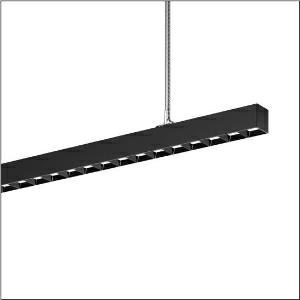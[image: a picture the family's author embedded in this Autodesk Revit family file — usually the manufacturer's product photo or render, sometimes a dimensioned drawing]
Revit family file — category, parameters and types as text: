
# Revit family: silica_r__21_51mx32dc4dbb_b922
name_source: partatom
category: Lighting Fixtures
units: mm (PartAtom-declared; Revit-internal decimal feet)

## family parameters
Cut with Voids When Loaded = No
Host = Face
Light Source = No
Part Type = Normal
Room Calculation Point = No
Round Connector Dimension = Use Diameter
Shared = No

## types (1)
- --- (1 x LED, 18230 lm, 105.8 W, 4000K)
    Apparent Load = 106 VA
    CIE Flux Codes = 86 99 100 59 100
    Color Rendering = 80
    Color Temperature = 4000K
    Default Elevation = 1800 mm
    Description = Silica® 21, office luminaire, primary light control with darklight reflector, of PMMA, black, CAT 2 (L<= 3000cd/m²), light emission: direct/indirect distribution, primary light characteristic: symmetric, installation type: suspended mounting, LED, rated luminous flux: 18.230lm, luminous efficacy: 172lm/W, light colour: 840, colour temperature: 4000K, with terminal, 3+2-pole, max. 2.5mm², mains connection: 220..240V, AC, 50/60Hz, rated input power: 105.8W, luminaire housing, of aluminium, jet black (RAL 9005), length: 3.004mm, width: 53mm, height: 53mm, protection rating (complete): IP20, insulation class (complete): insulation class I (protective earthing), certification: CE, permissible operating ambient temperature: 0..+35°C, standard: EN 50419, packaging unit: 1 piece
    Height = 53 mm
    Lamp = 1 x LED
    Lamp Light Flux = 18230 lm
    Lamp Power = 105.8 W
    Lamp count = 1
    Length = 3004 mm
    Luminous efficacy = 172 lm/W
    Manufacturer = Siteco
    ModVariant = No
    Model = 51MX32DC4DBB
    Mounting Place = Ceiling
    Mounting Type = Pendant
    Number of Poles = 1
    OnlyDefault = Yes
    Power Factor = 1
    Product Name = Silica® 21
    Product group = office luminaire | ceiling pendant
    ProductGroupID = 902
    Protection Class = Protection class I
    Protection Degree = IP 20
    RLX_Detail_Level = 1
    RLX_Emergency_Light_Flux = 0 lm
    RLX_Emergency_Type = 0
    RLX_Emergency_Type_DB = No
    RlxData = <blob elided: 66673 chars, md5=6024d63f>
    Socket = socket
    Standby Power = 0 W
    System Light Flux = 18230 lm
    System Power = 106 W
    Type Comments = factory setting: luminous flux: 100 % | dim-lin: 254 | 366 mA
    Type Image = l_1313617.jpg
    URL = http://relux.com
    VarID = @adj_070963
    Voltage = 0 V
    Weight = 0.00 kg
    Width = 53 mm

## geometry (parser evidence)
native form markers: Blend x4, Sweep x12
no freeform markers — native parametric forms only
